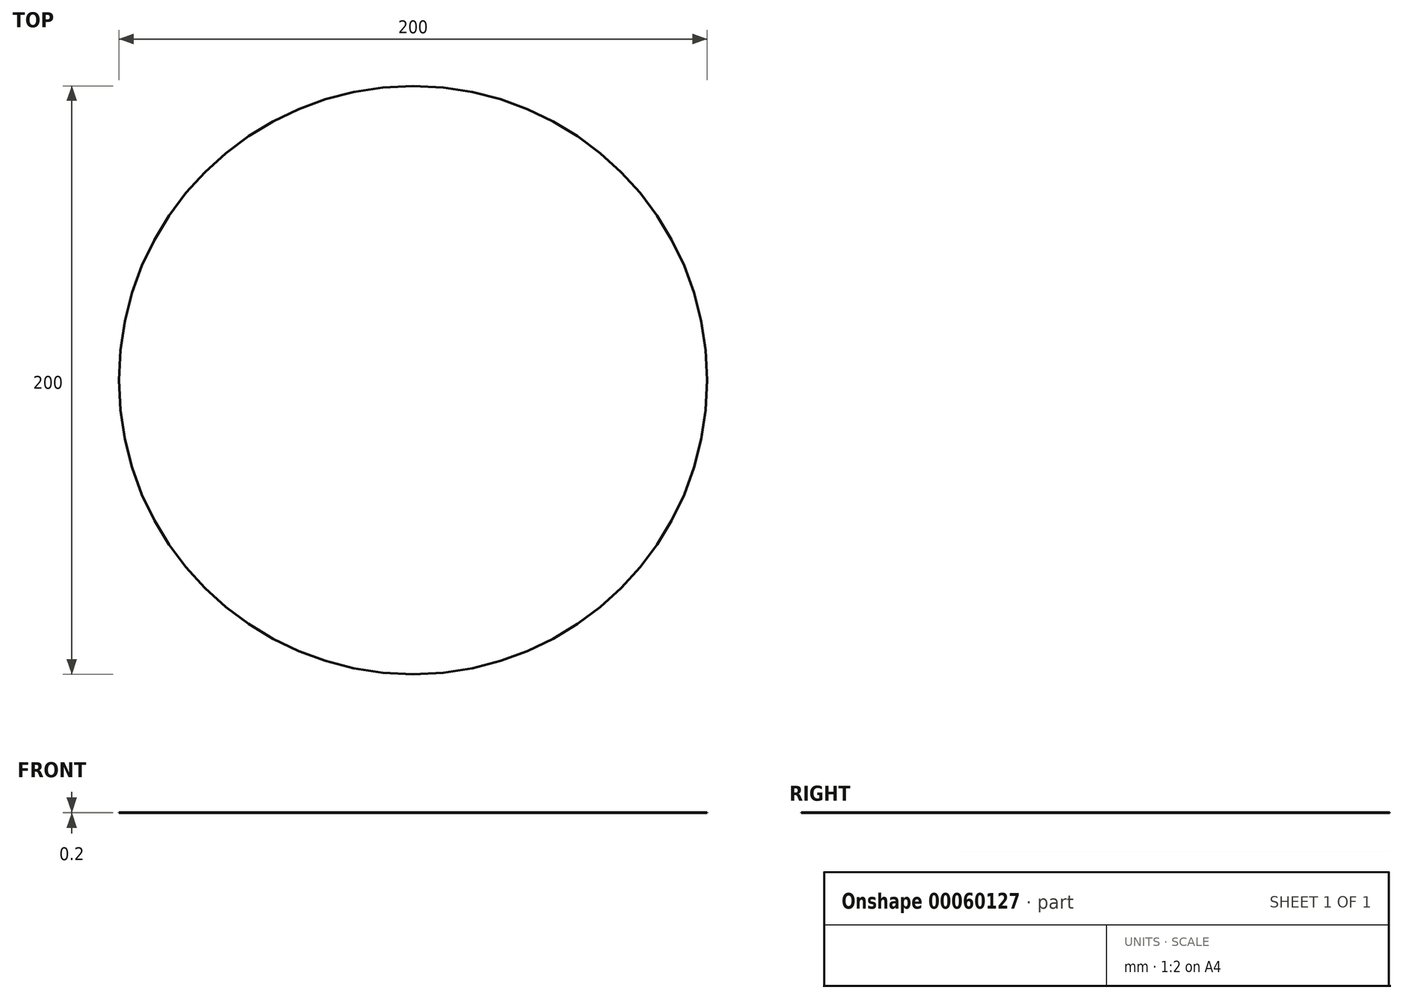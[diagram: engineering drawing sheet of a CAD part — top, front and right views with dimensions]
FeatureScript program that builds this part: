
annotation { "Feature Type Name" : "Feature", "Feature Type Description" : "" }
export const myFeature = defineFeature(function(context is Context, id is Id, definition is map)
    precondition{}
    {
        {
            var Q0;
            Q0=qCreatedBy(makeId("Top.planeOp"),FACE);
            var sketch = newSketch(context, id + "F0", { "sketchPlane" : qUnion([Q0])});
            skCircle(sketch, "E0", {"center": v(0, 0) * mm, "radius": 100 * mm});
            skSolve(sketch);
        }
        {
            var Q0;
            Q0=makeQuery(id+"F0.imprint","IMPRINT",FACE,{"disambiguationData":[TD([[makeQuery(id+"F0.imprint","IMPRINT",EDGE,{"derivedFrom":sQuery(id+"F0.wireOp",EDGE,"E0")}),1.0]])]});
            extrude(context, id + "F1", {"entities" : qUnion([Q0]), "depth" : 0.2 * mm});
        }
    });
